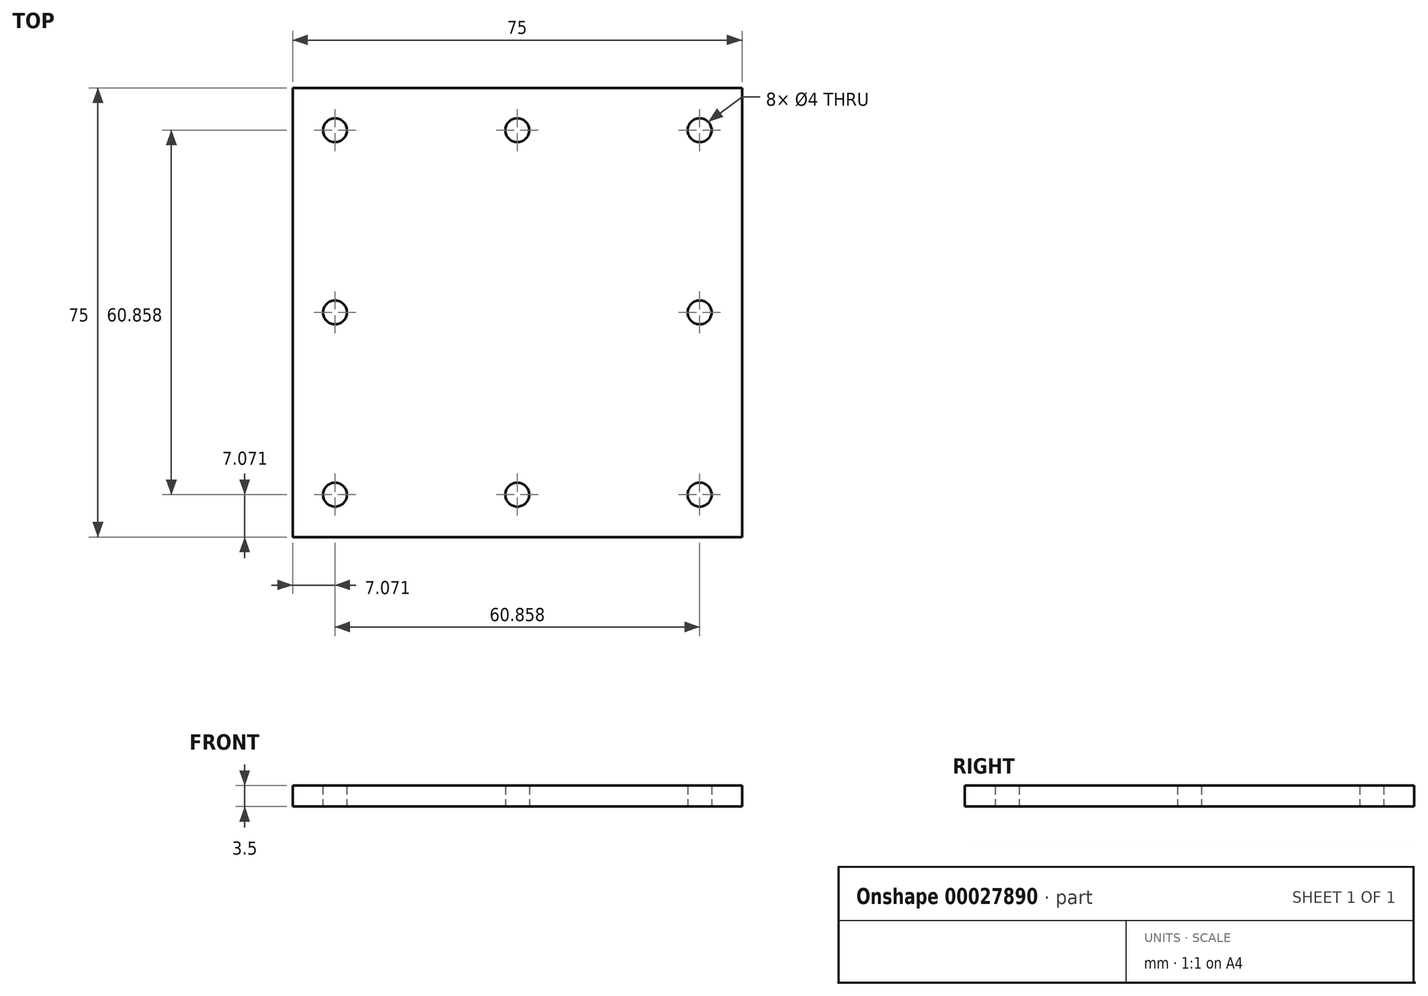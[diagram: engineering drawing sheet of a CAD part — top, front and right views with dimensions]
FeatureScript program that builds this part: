
annotation { "Feature Type Name" : "Feature", "Feature Type Description" : "" }
export const myFeature = defineFeature(function(context is Context, id is Id, definition is map)
    precondition{}
    {
        {
            var Q0;
            Q0=qCreatedBy(makeId("Top.planeOp"),FACE);
            var sketch = newSketch(context, id + "F0", { "sketchPlane" : qUnion([Q0])});
            skLineSegment(sketch, "E0.rect.bottom", {"start": v(37.5, -37.5) * mm, "end": v(-37.5, -37.5) * mm});
            skLineSegment(sketch, "E0.rect.top", {"start": v(37.5, 37.5) * mm, "end": v(-37.5, 37.5) * mm});
            skLineSegment(sketch, "E0.rect.left", {"start": v(37.5, -37.5) * mm, "end": v(37.5, 37.5) * mm});
            skLineSegment(sketch, "E0.rect.right", {"start": v(-37.5, -37.5) * mm, "end": v(-37.5, 37.5) * mm});
            skPoint(sketch, "E0.rect.middle", {"position": v(0, 0) * mm});
            skLineSegment(sketch, "E1", {"start": v(-37.5, -37.5) * mm, "end": v(37.5, 37.5) * mm, "construction": true});
            skLineSegment(sketch, "E2", {"start": v(37.5, -37.5) * mm, "end": v(-37.5, 37.5) * mm, "construction": true});
            skCircle(sketch, "E3", {"center": v(30.43, 30.43) * mm, "radius": 2 * mm});
            skLineSegment(sketch, "E4", {"start": v(30.43, 30.43) * mm, "end": v(37.5, 37.5) * mm, "construction": true});
            skCircle(sketch, "E5.1.0", {"center": v(-30.43, 30.43) * mm, "radius": 2 * mm});
            skCircle(sketch, "E5.2.0", {"center": v(-30.43, -30.43) * mm, "radius": 2 * mm});
            skCircle(sketch, "E5.3.0", {"center": v(30.43, -30.43) * mm, "radius": 2 * mm});
            skLineSegment(sketch, "E6", {"start": v(0, 37.5) * mm, "end": v(0, -37.5) * mm, "construction": true});
            skLineSegment(sketch, "E7", {"start": v(-37.5, 0) * mm, "end": v(37.5, 0) * mm, "construction": true});
            skCircle(sketch, "E8", {"center": v(0, 30.43) * mm, "radius": 2 * mm});
            skCircle(sketch, "E9.MirrorC", {"center": v(0, -30.43) * mm, "radius": 2 * mm});
            skCircle(sketch, "E10", {"center": v(30.43, 0) * mm, "radius": 2 * mm});
            skCircle(sketch, "E11.MirrorC", {"center": v(-30.43, 0) * mm, "radius": 2 * mm});
            skSolve(sketch);
        }
        {
            var Q0;
            Q0 = qSketchRegion(id + "F0", true);
            extrude(context, id + "F1", {"entities" : qUnion([Q0]), "depth" : 3.5 * mm});
        }
    });
